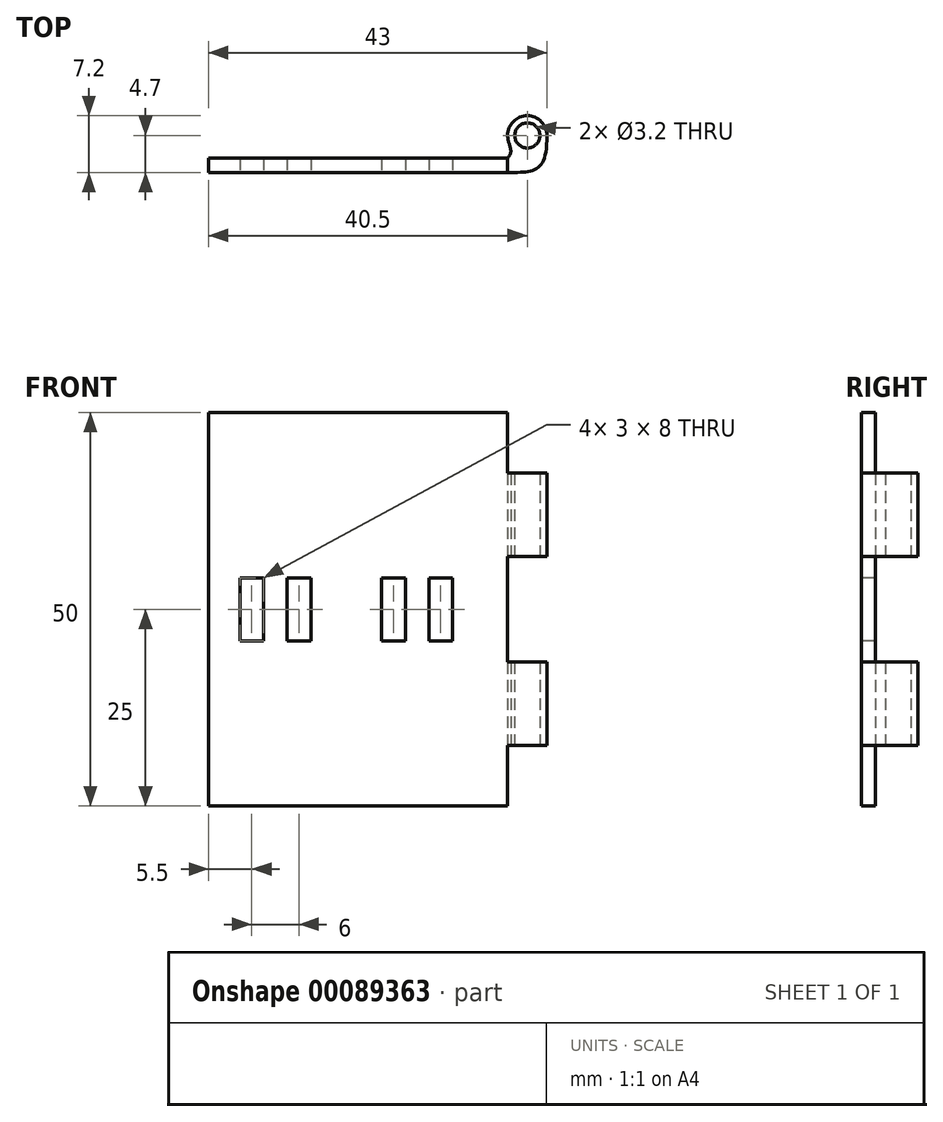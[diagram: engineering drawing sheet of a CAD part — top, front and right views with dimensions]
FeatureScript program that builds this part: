
annotation { "Feature Type Name" : "Feature", "Feature Type Description" : "" }
export const myFeature = defineFeature(function(context is Context, id is Id, definition is map)
    precondition{}
    {
        {
            var Q0;
            Q0=qCreatedBy(makeId("Top.planeOp"),FACE);
            var sketch = newSketch(context, id + "F0", { "sketchPlane" : qUnion([Q0])});
            skLineSegment(sketch, "E0.bottom", {"start": v(-38, 0.9) * mm, "end": v(0, 0.9) * mm});
            skLineSegment(sketch, "E0.top", {"start": v(-38, -0.9) * mm, "end": v(0, -0.9) * mm});
            skLineSegment(sketch, "E0.left", {"start": v(-38, 0.9) * mm, "end": v(-38, -0.9) * mm});
            skLineSegment(sketch, "E0.right", {"start": v(0, 0.9) * mm, "end": v(0, -0.9) * mm});
            skPoint(sketch, "E1", {"position": v(0, 0) * mm});
            skCircle(sketch, "E2", {"center": v(2.5, 3.8) * mm, "radius": 2.5 * mm, "construction": true});
            skLineSegment(sketch, "E3", {"start": v(-2.17, 0.9) * mm, "end": v(14.96, 0.9) * mm, "construction": true});
            skLineSegment(sketch, "E4", {"start": v(0, -0.9) * mm, "end": v(0, 7.5) * mm, "construction": true});
            skLineSegment(sketch, "E5", {"start": v(0, 3.8) * mm, "end": v(7.58, 3.8) * mm, "construction": true});
            skLineSegment(sketch, "E6", {"start": v(5, 0.9) * mm, "end": v(5, 3.83) * mm, "construction": true});
            skArc(sketch, "E7", {"start": v(5, 3.8) * mm, "mid": v(2.5, 6.3) * mm, "end": v(0, 3.8) * mm});
            skFitSpline(sketch, "E8", {"points": [v(0, -0.9) * mm, v(5, 3.8) * mm], "startDerivative": vector(10.17, 0) * mm, "endDerivative": vector(0, 14.45) * mm});
            skLineSegment(sketch, "E9", {"start": v(5, 3.8) * mm, "end": v(5, -1.02) * mm, "construction": true});
            skLineSegment(sketch, "E10", {"start": v(0, -0.9) * mm, "end": v(3.39, -0.9) * mm, "construction": true});
            skCircle(sketch, "E11", {"center": v(2.5, 3.8) * mm, "radius": 1.6 * mm});
            skFitSpline(sketch, "E12", {"points": [v(0, 3.8) * mm, v(0, 0.9) * mm], "startDerivative": vector(0, -3.6) * mm, "endDerivative": vector(-2.7, -2.93) * mm});
            skLineSegment(sketch, "E13", {"start": v(-3.15, 1.3) * mm, "end": v(10.6, 1.3) * mm, "construction": true});
            skSolve(sketch);
        }
        {
            var Q0;
            Q0 = qSketchRegion(id + "F0", true);
            extrude(context, id + "F1", {"entities" : qUnion([Q0]), "depth" : 50 * mm});
        }
        {
            var Q0;
            Q0=qCreatedBy(makeId("Right.planeOp"),FACE);
            var sketch = newSketch(context, id + "F2", { "sketchPlane" : qUnion([Q0])});
            skLineSegment(sketch, "E14.bottom", {"start": v(-18.44, 7.7) * mm, "end": v(21.06, 7.7) * mm});
            skLineSegment(sketch, "E14.top", {"start": v(-18.44, 0) * mm, "end": v(21.06, 0) * mm});
            skLineSegment(sketch, "E14.left", {"start": v(-18.44, 7.7) * mm, "end": v(-18.44, 0) * mm});
            skLineSegment(sketch, "E14.right", {"start": v(21.06, 7.7) * mm, "end": v(21.06, 0) * mm});
            skLineSegment(sketch, "E15.bottom", {"start": v(-19.4, 31.7) * mm, "end": v(20.1, 31.7) * mm});
            skLineSegment(sketch, "E15.top", {"start": v(-19.4, 18.3) * mm, "end": v(20.1, 18.3) * mm});
            skLineSegment(sketch, "E15.left", {"start": v(-19.4, 31.7) * mm, "end": v(-19.4, 18.3) * mm});
            skLineSegment(sketch, "E15.right", {"start": v(20.1, 31.7) * mm, "end": v(20.1, 18.3) * mm});
            skLineSegment(sketch, "E16.bottom", {"start": v(-31.63, 73.85) * mm, "end": v(27.62, 73.85) * mm});
            skLineSegment(sketch, "E16.top", {"start": v(-31.63, 42.3) * mm, "end": v(27.62, 42.3) * mm});
            skLineSegment(sketch, "E16.left", {"start": v(-31.63, 73.85) * mm, "end": v(-31.63, 42.3) * mm});
            skLineSegment(sketch, "E16.right", {"start": v(27.62, 73.85) * mm, "end": v(27.62, 42.3) * mm});
            skSolve(sketch);
        }
        {
            var Q0;
            Q0 = qSketchRegion(id + "F2", true);
            extrude(context, id + "F3", {"entities" : qUnion([Q0]), "operationType" : NewBodyOperationType.REMOVE, "depth" : 25 * mm});
        }
        {
            var Q0;
            Q0=makeQuery(id+"F1.opExtrude","SWEPT_FACE",FACE,{"disambiguationData":[OSD([sQuery(id+"F0.wireOp",EDGE,"E0.top")])]});
            var sketch = newSketch(context, id + "F4", { "sketchPlane" : qUnion([Q0])});
            skLineSegment(sketch, "E17.bottom", {"start": v(-34, 29) * mm, "end": v(-31, 29) * mm});
            skLineSegment(sketch, "E17.top", {"start": v(-34, 21) * mm, "end": v(-31, 21) * mm});
            skLineSegment(sketch, "E17.left", {"start": v(-34, 29) * mm, "end": v(-34, 21) * mm});
            skLineSegment(sketch, "E17.right", {"start": v(-31, 29) * mm, "end": v(-31, 21) * mm});
            skLineSegment(sketch, "E18.1.0.0", {"start": v(-25, 29) * mm, "end": v(-25, 21) * mm});
            skLineSegment(sketch, "E18.1.0.1", {"start": v(-28, 29) * mm, "end": v(-28, 21) * mm});
            skLineSegment(sketch, "E18.1.0.2", {"start": v(-28, 21) * mm, "end": v(-25, 21) * mm});
            skLineSegment(sketch, "E18.1.0.3", {"start": v(-28, 29) * mm, "end": v(-25, 29) * mm});
            skLineSegment(sketch, "E18.direction1", {"start": v(-31, 21) * mm, "end": v(-25, 21) * mm, "construction": true});
            skLineSegment(sketch, "E19.1.0.0", {"start": v(-13, 29) * mm, "end": v(-13, 21) * mm});
            skLineSegment(sketch, "E19.1.0.1", {"start": v(-16, 29) * mm, "end": v(-16, 21) * mm});
            skLineSegment(sketch, "E19.1.0.2", {"start": v(-10, 29) * mm, "end": v(-10, 21) * mm});
            skLineSegment(sketch, "E19.1.0.3", {"start": v(-7, 29) * mm, "end": v(-7, 21) * mm});
            skLineSegment(sketch, "E19.1.0.4", {"start": v(-16, 29) * mm, "end": v(-13, 29) * mm});
            skLineSegment(sketch, "E19.1.0.5", {"start": v(-16, 21) * mm, "end": v(-13, 21) * mm});
            skLineSegment(sketch, "E19.1.0.6", {"start": v(-10, 29) * mm, "end": v(-7, 29) * mm});
            skLineSegment(sketch, "E19.1.0.7", {"start": v(-10, 21) * mm, "end": v(-7, 21) * mm});
            skLineSegment(sketch, "E19.1.0.8", {"start": v(-13, 21) * mm, "end": v(-7, 21) * mm, "construction": true});
            skLineSegment(sketch, "E19.direction1", {"start": v(-31, 21) * mm, "end": v(-13, 21) * mm, "construction": true});
            skLineSegment(sketch, "E19.direction2", {"start": v(-31, 21) * mm, "end": v(-31, -27) * mm, "construction": true});
            skSolve(sketch);
        }
        {
            var Q0;
            Q0 = qSketchRegion(id + "F4", true);
            extrude(context, id + "F5", {"entities" : qUnion([Q0]), "operationType" : NewBodyOperationType.REMOVE, "endBound" : BoundingType.UP_TO_NEXT, "oppositeDirection" : true, "depth" : 25 * mm});
        }
    });
